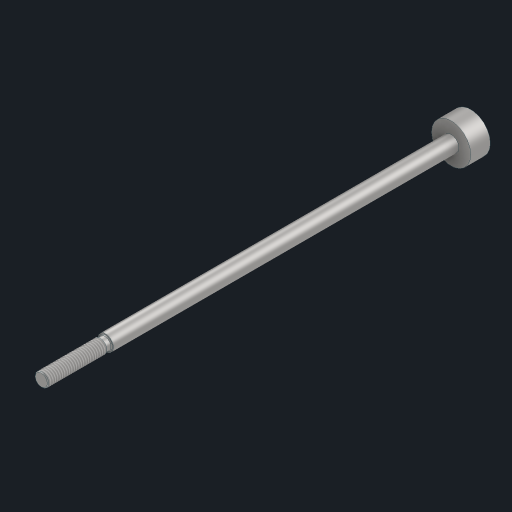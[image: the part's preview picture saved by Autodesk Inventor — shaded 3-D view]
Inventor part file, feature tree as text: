
AUTODESK INVENTOR PART (.ipt)
format: ipt  version: 2023 (Build 270158030, 158C)  size: 120,832 bytes
history: mixed  units: in
note: dims shown in document units (in); Inventor stores cm internally (conversion verified against a paired STEP export)
features: thread x2, imported_body x1
ambient origin geometry x8: Origin, YZ Plane, XZ Plane, XY Plane, X Axis, Y Axis, Z Axis, Center Point
bodies: Solid1 (imported_parasolid)
feature tree (3):
  thread  "Thread1"  [1 undecoded]
  thread  "Threads"  [1 undecoded]
  imported_body  NMx_Import_Brep_tag  [imported B-rep: ~11 faces, bbox_mm=[7.0, 0.0, 109.434]]
note: 2 required parameter values undecoded (feature->parameter linkage not recoverable at this tier; creation-order binding heuristic only, values carry confidence <= 0.55)
